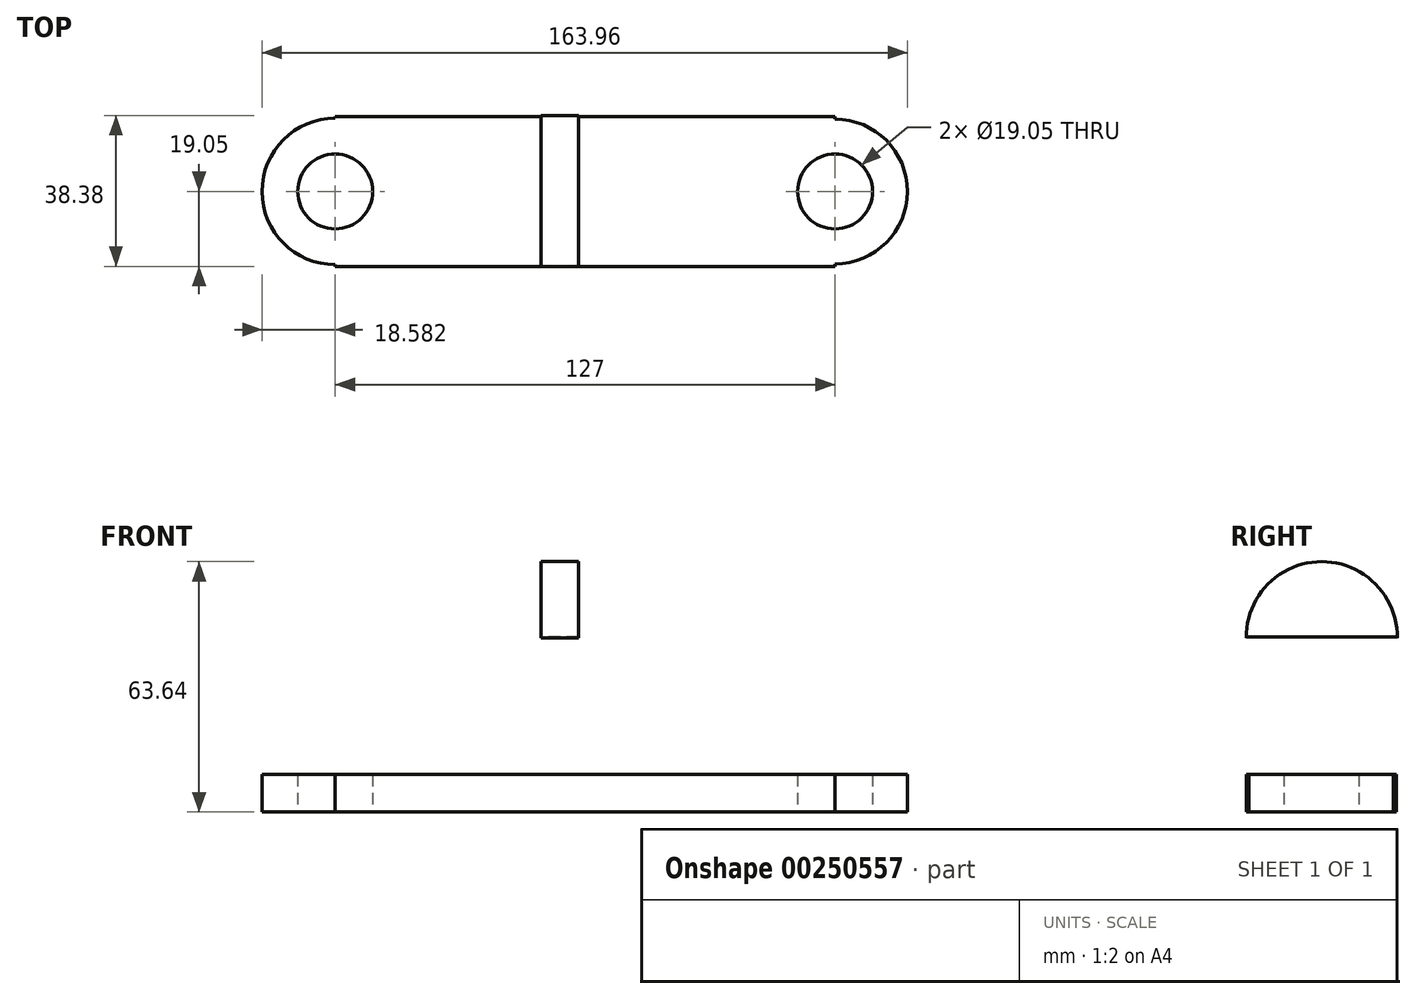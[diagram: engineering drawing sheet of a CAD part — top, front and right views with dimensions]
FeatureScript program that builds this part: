
annotation { "Feature Type Name" : "Feature", "Feature Type Description" : "" }
export const myFeature = defineFeature(function(context is Context, id is Id, definition is map)
    precondition{}
    {
        {
            var Q0;
            Q0=qCreatedBy(makeId("Top.planeOp"),FACE);
            var sketch = newSketch(context, id + "F0", { "sketchPlane" : qUnion([Q0])});
            skLineSegment(sketch, "E0", {"start": v(-52.3, 0) * mm, "end": v(-52.3, 0.47) * mm});
            skLineSegment(sketch, "E1", {"start": v(-52.3, 0) * mm, "end": v(74.7, 0) * mm});
            skLineSegment(sketch, "E2", {"start": v(74.7, 0) * mm, "end": v(74.7, 0.67) * mm});
            skLineSegment(sketch, "E3", {"start": v(74.7, 38.1) * mm, "end": v(-52.3, 38.1) * mm});
            skArc(sketch, "E4", {"start": v(-52.3, 37.63) * mm, "mid": v(-70.9, 19.05) * mm, "end": v(-52.3, 0.47) * mm});
            skLineSegment(sketch, "E5.trimOffspring", {"start": v(-52.3, 37.63) * mm, "end": v(-52.3, 38.1) * mm});
            skArc(sketch, "E6", {"start": v(74.7, 0.67) * mm, "mid": v(93.07, 19.05) * mm, "end": v(74.7, 37.43) * mm});
            skLineSegment(sketch, "E7.trimOffspring", {"start": v(74.7, 37.43) * mm, "end": v(74.7, 38.1) * mm});
            skCircle(sketch, "E8", {"center": v(-52.3, 19.05) * mm, "radius": 9.53 * mm});
            skCircle(sketch, "E9", {"center": v(74.7, 19.05) * mm, "radius": 9.53 * mm});
            skSolve(sketch);
        }
        {
            var Q0;
            Q0 = qSketchRegion(id + "F0", true);
            extrude(context, id + "F1", {"entities" : qUnion([Q0]), "depth" : 9.52 * mm});
        }
        {
            var Q0;
            Q0=qCreatedBy(makeId("Right.planeOp"),FACE);
            var sketch = newSketch(context, id + "F2", { "sketchPlane" : qUnion([Q0])});
            skLineSegment(sketch, "E10", {"start": v(0, 44.24) * mm, "end": v(0, 44.45) * mm});
            skPoint(sketch, "E11.end.orphan", {"position": v(0, 44.45) * mm});
            skPoint(sketch, "E11.start.orphan", {"position": v(38.38, 0) * mm});
            skLineSegment(sketch, "E12", {"start": v(38.38, 44.24) * mm, "end": v(38.38, 44.45) * mm});
            skArc(sketch, "E13", {"start": v(38.38, 44.24) * mm, "mid": v(19.2, 63.64) * mm, "end": v(0, 44.24) * mm});
            skLineSegment(sketch, "E14", {"start": v(0, 44.45) * mm, "end": v(38.38, 44.45) * mm});
            skLineSegment(sketch, "E15", {"start": v(37.76, 10.37) * mm, "end": v(38.38, 44.45) * mm});
            skLineSegment(sketch, "E16", {"start": v(0, 10.06) * mm, "end": v(0, 44.45) * mm});
            skSolve(sketch);
        }
        {
            var Q0;
            Q0=makeQuery(id+"F2.imprint","IMPRINT",FACE,{"disambiguationData":[TD([[makeQuery(id+"F2.imprint","IMPRINT",EDGE,{"derivedFrom":sQuery(id+"F2.wireOp",EDGE,"E12")}),-1.0]])]});
            extrude(context, id + "F3", {"entities" : qUnion([Q0]), "depth" : 9.52 * mm});
        }
    });
